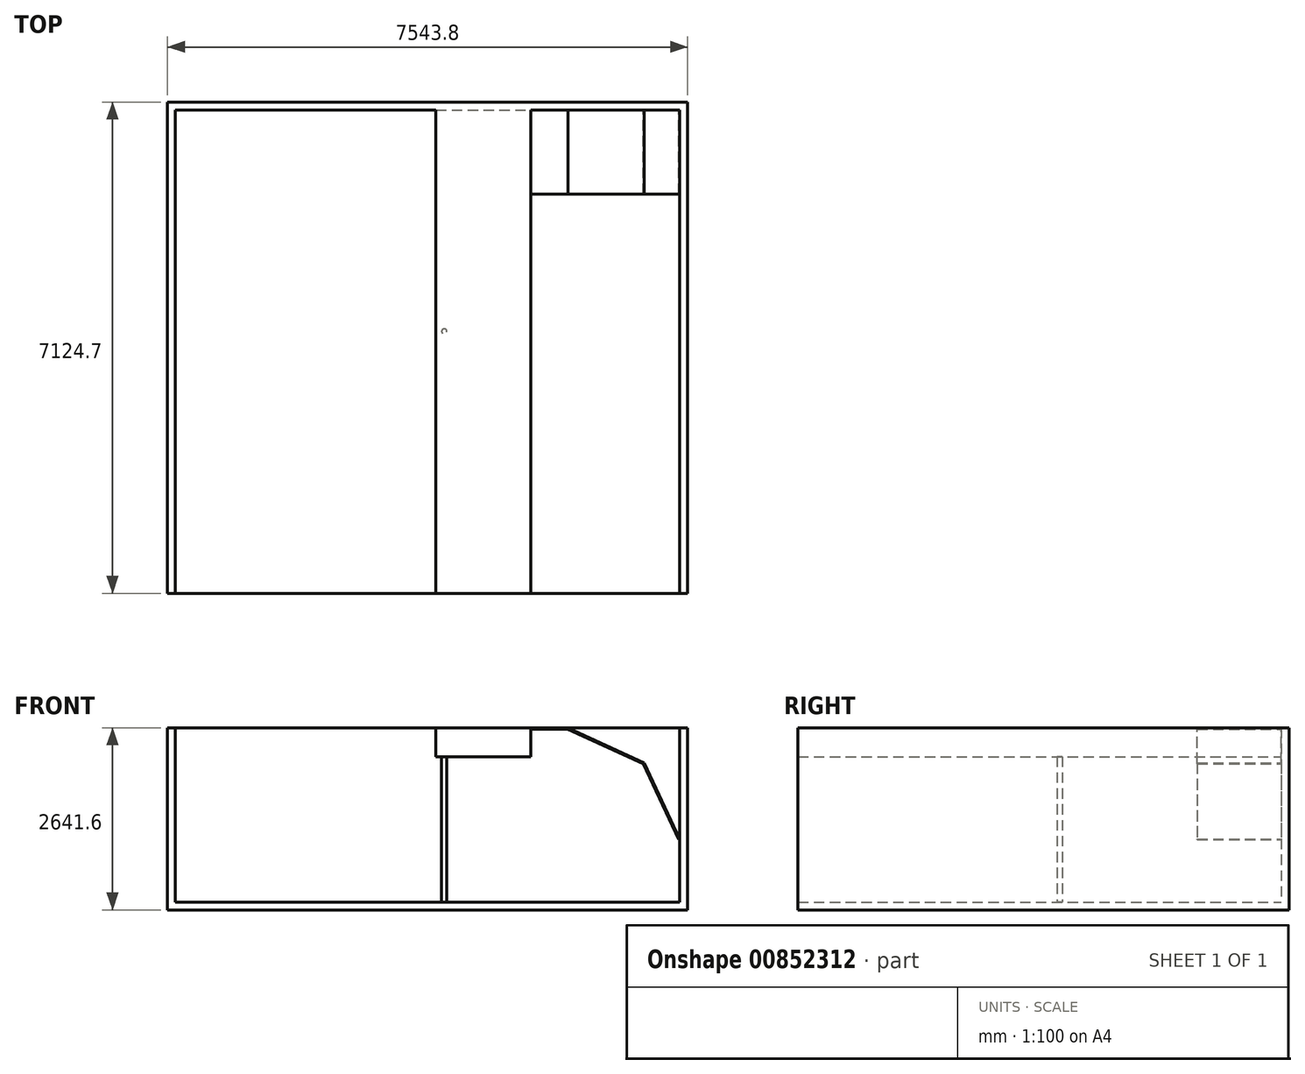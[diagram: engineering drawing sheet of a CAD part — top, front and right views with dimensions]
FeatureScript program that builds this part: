
annotation { "Feature Type Name" : "Feature", "Feature Type Description" : "" }
export const myFeature = defineFeature(function(context is Context, id is Id, definition is map)
    precondition{}
    {
        {
            var Q0;
            Q0=qCreatedBy(makeId("Front.planeOp"),FACE);
            var sketch = newSketch(context, id + "F0", { "sketchPlane" : qUnion([Q0])});
            skLineSegment(sketch, "E0.bottom", {"start": v(3771.9, 0) * mm, "end": v(-3771.9, 0) * mm});
            skLineSegment(sketch, "E0.top", {"start": v(3771.9, 2641.6) * mm, "end": v(-3771.9, 2641.6) * mm});
            skLineSegment(sketch, "E0.left", {"start": v(3771.9, 0) * mm, "end": v(3771.9, 2641.6) * mm});
            skLineSegment(sketch, "E0.right", {"start": v(-3771.9, 0) * mm, "end": v(-3771.9, 2641.6) * mm});
            skPoint(sketch, "E0.middle", {"position": v(0, 1320.8) * mm});
            skSolve(sketch);
        }
        {
            var Q0;
            Q0 = qSketchRegion(id + "F0", true);
            extrude(context, id + "F1", {"entities" : qUnion([Q0]), "depth" : 114.3 * mm, "offsetDistance" : 25.4 * mm});
        }
        {
            var Q0;
            Q0=makeQuery(id+"F1.opExtrude","CAP_FACE",FACE,{"disambiguationData":[OSD([sQuery(id+"F0.wireOp",EDGE,"E0.bottom"),sQuery(id+"F0.wireOp",EDGE,"E0.top"),sQuery(id+"F0.wireOp",EDGE,"E0.left"),sQuery(id+"F0.wireOp",EDGE,"E0.right")])],"isStart":false});
            var sketch = newSketch(context, id + "F2", { "sketchPlane" : qUnion([Q0])});
            skLineSegment(sketch, "E1.bottom", {"start": v(-3771.9, 0) * mm, "end": v(3771.9, 0) * mm});
            skLineSegment(sketch, "E1.top", {"start": v(-3771.9, 114.3) * mm, "end": v(3771.9, 114.3) * mm});
            skLineSegment(sketch, "E1.left", {"start": v(-3771.9, 0) * mm, "end": v(-3771.9, 114.3) * mm});
            skLineSegment(sketch, "E1.right", {"start": v(3771.9, 0) * mm, "end": v(3771.9, 114.3) * mm});
            skSolve(sketch);
        }
        {
            var Q0;
            Q0=makeQuery(id+"F1.opExtrude","CAP_FACE",FACE,{"disambiguationData":[OSD([sQuery(id+"F0.wireOp",EDGE,"E0.bottom"),sQuery(id+"F0.wireOp",EDGE,"E0.top"),sQuery(id+"F0.wireOp",EDGE,"E0.left"),sQuery(id+"F0.wireOp",EDGE,"E0.right")])],"isStart":false});
            var sketch = newSketch(context, id + "F3", { "sketchPlane" : qUnion([Q0])});
            skLineSegment(sketch, "E2.bottom", {"start": v(3771.9, 2641.6) * mm, "end": v(3657.6, 2641.6) * mm});
            skLineSegment(sketch, "E2.top", {"start": v(3771.9, 114.3) * mm, "end": v(3657.6, 114.3) * mm});
            skLineSegment(sketch, "E2.left", {"start": v(3771.9, 2641.6) * mm, "end": v(3771.9, 114.3) * mm});
            skLineSegment(sketch, "E2.right", {"start": v(3657.6, 2641.6) * mm, "end": v(3657.6, 114.3) * mm});
            skSolve(sketch);
        }
        {
            var Q0;
            Q0=makeQuery(id+"F1.opExtrude","CAP_FACE",FACE,{"disambiguationData":[OSD([sQuery(id+"F0.wireOp",EDGE,"E0.bottom"),sQuery(id+"F0.wireOp",EDGE,"E0.top"),sQuery(id+"F0.wireOp",EDGE,"E0.left"),sQuery(id+"F0.wireOp",EDGE,"E0.right")])],"isStart":false});
            var sketch = newSketch(context, id + "F4", { "sketchPlane" : qUnion([Q0])});
            skLineSegment(sketch, "E3.bottom", {"start": v(-3771.9, 2641.6) * mm, "end": v(-3657.6, 2641.6) * mm});
            skLineSegment(sketch, "E3.top", {"start": v(-3771.9, 114.3) * mm, "end": v(-3657.6, 114.3) * mm});
            skLineSegment(sketch, "E3.left", {"start": v(-3771.9, 2641.6) * mm, "end": v(-3771.9, 114.3) * mm});
            skLineSegment(sketch, "E3.right", {"start": v(-3657.6, 2641.6) * mm, "end": v(-3657.6, 114.3) * mm});
            skSolve(sketch);
        }
        {
            var Q0;
            Q0=makeQuery(id+"F1.opExtrude","CAP_FACE",FACE,{"disambiguationData":[OSD([sQuery(id+"F0.wireOp",EDGE,"E0.bottom"),sQuery(id+"F0.wireOp",EDGE,"E0.top"),sQuery(id+"F0.wireOp",EDGE,"E0.left"),sQuery(id+"F0.wireOp",EDGE,"E0.right")])],"isStart":false});
            var sketch = newSketch(context, id + "F5", { "sketchPlane" : qUnion([Q0])});
            skLineSegment(sketch, "E4.bottom", {"start": v(120.65, 2641.6) * mm, "end": v(1498.6, 2641.6) * mm});
            skLineSegment(sketch, "E4.top", {"start": v(120.65, 2222.5) * mm, "end": v(1498.6, 2222.5) * mm});
            skLineSegment(sketch, "E4.left", {"start": v(120.65, 2641.6) * mm, "end": v(120.65, 2222.5) * mm});
            skLineSegment(sketch, "E4.right", {"start": v(1498.6, 2641.6) * mm, "end": v(1498.6, 2222.5) * mm});
            skSolve(sketch);
        }
        {
            var Q0;
            Q0 = qSketchRegion(id + "F2", true);
            var Q1;
            Q1 = qSketchRegion(id + "F3", true);
            var Q2;
            Q2 = qSketchRegion(id + "F4", true);
            var Q3;
            Q3 = qSketchRegion(id + "F5", true);
            extrude(context, id + "F6", {"entities" : qUnion([Q0, Q1, Q2, Q3]), "operationType" : NewBodyOperationType.ADD, "depth" : 7010.4 * mm, "offsetDistance" : 25.4 * mm});
        }
        {
            var Q0;
            Q0=makeQuery(id+"F1.opExtrude","CAP_FACE",FACE,{"disambiguationData":[OSD([sQuery(id+"F0.wireOp",EDGE,"E0.bottom"),sQuery(id+"F0.wireOp",EDGE,"E0.top"),sQuery(id+"F0.wireOp",EDGE,"E0.left"),sQuery(id+"F0.wireOp",EDGE,"E0.right")])],"isStart":false});
            var sketch = newSketch(context, id + "F7", { "sketchPlane" : qUnion([Q0])});
            skLineSegment(sketch, "E5", {"start": v(3142.34, 2133.67) * mm, "end": v(3657.6, 1028.7) * mm});
            skLineSegment(sketch, "E6", {"start": v(3142.34, 2133.67) * mm, "end": v(2033.99, 2641.6) * mm});
            skLineSegment(sketch, "E7.0", {"start": v(3128.04, 2119.27) * mm, "end": v(2029.83, 2622.55) * mm});
            skLineSegment(sketch, "E8.0", {"start": v(3128.04, 2119.27) * mm, "end": v(3640.33, 1020.65) * mm});
            skLineSegment(sketch, "E9", {"start": v(3640.33, 1020.65) * mm, "end": v(3657.6, 1028.7) * mm});
            skLineSegment(sketch, "E10.bottom", {"start": v(1498.6, 2641.6) * mm, "end": v(2033.99, 2641.6) * mm});
            skLineSegment(sketch, "E10.top", {"start": v(1498.6, 2622.55) * mm, "end": v(2029.83, 2622.55) * mm});
            skLineSegment(sketch, "E10.left", {"start": v(1498.6, 2641.6) * mm, "end": v(1498.6, 2622.55) * mm});
            skSolve(sketch);
        }
        {
            var Q0;
            Q0 = qSketchRegion(id + "F7", true);
            extrude(context, id + "F8", {"entities" : qUnion([Q0]), "depth" : 1219.2 * mm, "offsetDistance" : 25.4 * mm});
        }
        {
            var Q0;
            Q0=makeQuery(id+"F6.opExtrude","SWEPT_FACE",FACE,{"disambiguationData":[OSD([sQuery(id+"F2.wireOp",EDGE,"E1.top")])]});
            var sketch = newSketch(context, id + "F9", { "sketchPlane" : qUnion([Q0])});
            skCircle(sketch, "E11", {"center": v(241.3, -3327.4) * mm, "radius": 38.1 * mm});
            skSolve(sketch);
        }
        {
            var Q0;
            Q0 = qSketchRegion(id + "F9", true);
            extrude(context, id + "F10", {"entities" : qUnion([Q0]), "operationType" : NewBodyOperationType.ADD, "depth" : 2108.2 * mm, "offsetDistance" : 25.4 * mm});
        }
    });
